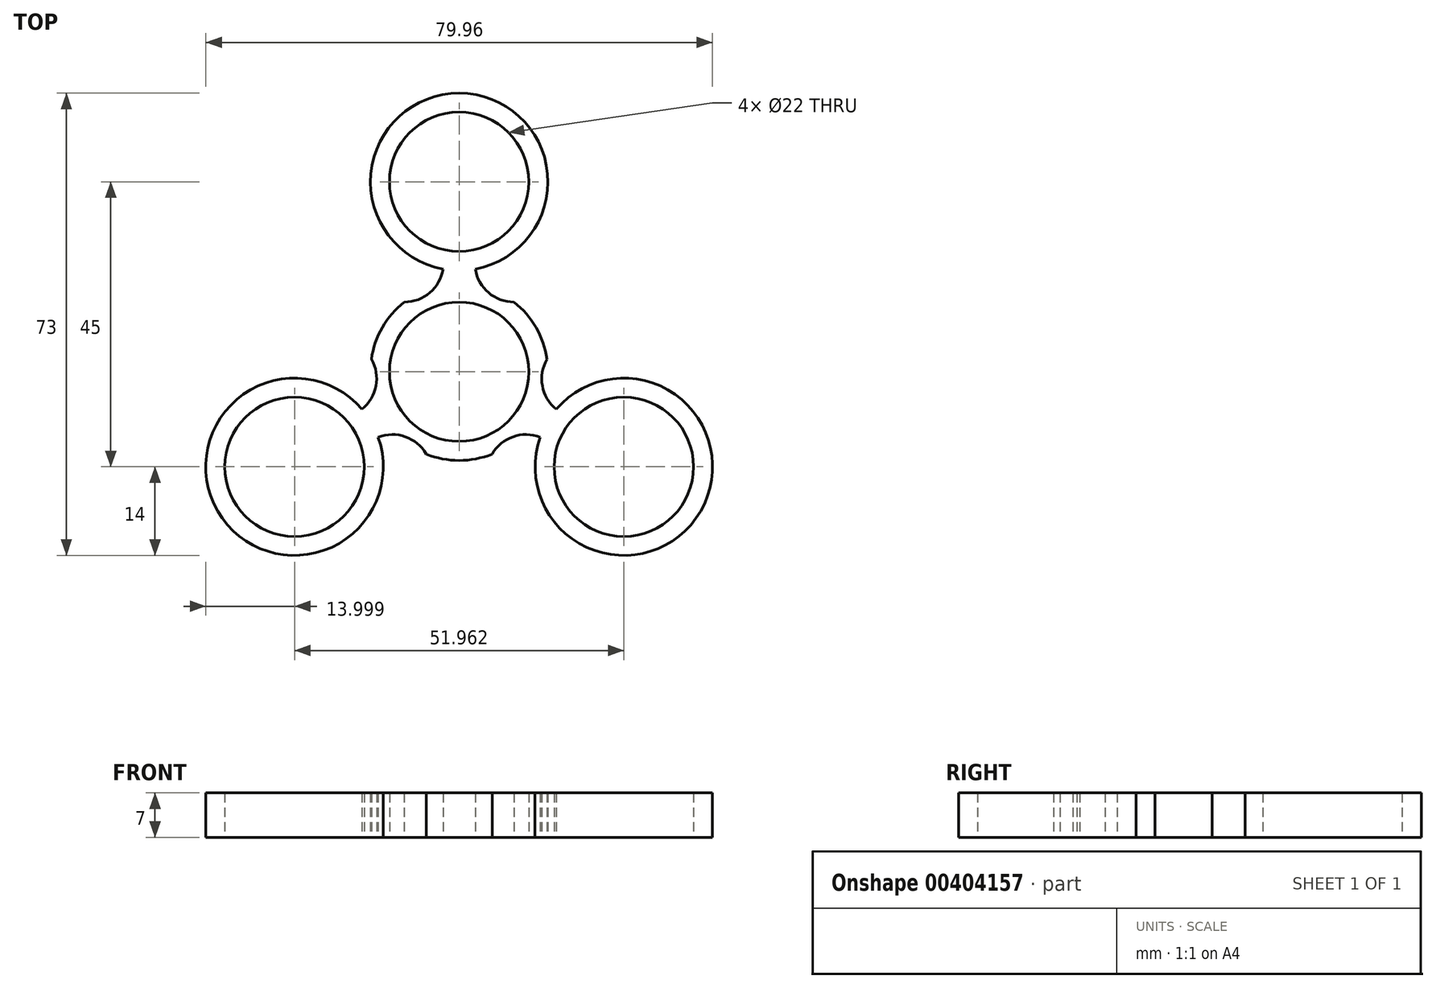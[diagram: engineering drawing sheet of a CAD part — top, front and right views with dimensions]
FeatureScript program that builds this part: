
annotation { "Feature Type Name" : "Feature", "Feature Type Description" : "" }
export const myFeature = defineFeature(function(context is Context, id is Id, definition is map)
    precondition{}
    {
        {
            var Q0;
            Q0=qCreatedBy(makeId("Top.planeOp"),FACE);
            var sketch = newSketch(context, id + "F0", { "sketchPlane" : qUnion([Q0])});
            skCircle(sketch, "E0", {"center": v(0, 0) * mm, "radius": 11 * mm});
            skCircle(sketch, "E1", {"center": v(0, 30) * mm, "radius": 11 * mm});
            skCircle(sketch, "E2.0", {"center": v(0, 30) * mm, "radius": 14 * mm});
            skLineSegment(sketch, "E3", {"start": v(0, 16.23) * mm, "end": v(-2.54, 16.23) * mm});
            skLineSegment(sketch, "E4.MirrorCS", {"start": v(0, 16.23) * mm, "end": v(2.54, 16.23) * mm});
            skArc(sketch, "E5", {"start": v(-8.66, 11) * mm, "mid": v(-5.87, 11.66) * mm, "end": v(-3.68, 13.5) * mm});
            skArc(sketch, "E6.MirrorCS", {"start": v(8.66, 11) * mm, "mid": v(4.63, 12.49) * mm, "end": v(2.54, 16.23) * mm});
            skArc(sketch, "E7", {"start": v(-3.68, 13.5) * mm, "mid": v(-2.95, 14.8) * mm, "end": v(-2.54, 16.23) * mm});
            skArc(sketch, "E8", {"start": v(-8.66, 11) * mm, "mid": v(-12.12, 7) * mm, "end": v(-13.86, 2) * mm});
            skCircle(sketch, "E9.1.0", {"center": v(-25.98, -15) * mm, "radius": 11 * mm});
            skArc(sketch, "E9.1.2", {"start": v(-5.2, -13) * mm, "mid": v(-7.16, -10.92) * mm, "end": v(-9.86, -9.94) * mm});
            skArc(sketch, "E9.1.3", {"start": v(-13.86, 2) * mm, "mid": v(-13.13, -2.23) * mm, "end": v(-15.33, -5.91) * mm});
            skCircle(sketch, "E9.1.5", {"center": v(-25.98, -15) * mm, "radius": 14 * mm});
            skLineSegment(sketch, "E9.1.6", {"start": v(-14.06, -8.12) * mm, "end": v(-12.79, -10.32) * mm});
            skLineSegment(sketch, "E9.1.7", {"start": v(-14.06, -8.12) * mm, "end": v(-15.33, -5.91) * mm});
            skArc(sketch, "E9.1.8", {"start": v(-9.86, -9.94) * mm, "mid": v(-11.34, -9.95) * mm, "end": v(-12.79, -10.32) * mm});
            skCircle(sketch, "E9.2.0", {"center": v(25.98, -15) * mm, "radius": 11 * mm});
            skArc(sketch, "E9.2.2", {"start": v(13.86, 2) * mm, "mid": v(13.04, -0.74) * mm, "end": v(13.54, -3.56) * mm});
            skArc(sketch, "E9.2.3", {"start": v(5.2, -13) * mm, "mid": v(8.5, -10.26) * mm, "end": v(12.79, -10.32) * mm});
            skCircle(sketch, "E9.2.5", {"center": v(25.98, -15) * mm, "radius": 14 * mm});
            skLineSegment(sketch, "E9.2.6", {"start": v(14.06, -8.12) * mm, "end": v(15.33, -5.91) * mm});
            skLineSegment(sketch, "E9.2.7", {"start": v(14.06, -8.12) * mm, "end": v(12.79, -10.32) * mm});
            skLineSegment(sketch, "E9.2.8", {"start": v(13.54, -3.56) * mm, "end": v(13.54, -3.56) * mm});
            skArc(sketch, "E10", {"start": v(13.86, 2) * mm, "mid": v(12.12, 7) * mm, "end": v(8.66, 11) * mm});
            skArc(sketch, "E11", {"start": v(13.54, -3.56) * mm, "mid": v(14.3, -4.85) * mm, "end": v(15.33, -5.91) * mm});
            skArc(sketch, "E12", {"start": v(-5.2, -13) * mm, "mid": v(0, -14) * mm, "end": v(5.2, -13) * mm});
            skSolve(sketch);
        }
        {
            var Q0;
            {var subQ2=sQuery(id+"F0.wireOp",EDGE,"E9.2.6");Q0=makeQuery(id+"F0.imprint","IMPRINT",FACE,{"disambiguationData":[TD([[makeQuery(id+"F0.imprint","IMPRINT",EDGE,{"derivedFrom":subQ2}),1.0]])]});}
            var Q1;
            Q1=makeQuery(id+"F0.imprint","IMPRINT",FACE,{"disambiguationData":[TD([[makeQuery(id+"F0.imprint","IMPRINT",EDGE,{"derivedFrom":sQuery(id+"F0.wireOp",EDGE,"E9.2.0")}),-1.0]])]});
            var Q2;
            Q2=makeQuery(id+"F0.imprint","IMPRINT",FACE,{"disambiguationData":[TD([[makeQuery(id+"F0.imprint","IMPRINT",EDGE,{"derivedFrom":sQuery(id+"F0.wireOp",EDGE,"E0")}),-1.0]])]});
            var Q3;
            {var subQ2=sQuery(id+"F0.wireOp",EDGE,"E9.1.6");Q3=makeQuery(id+"F0.imprint","IMPRINT",FACE,{"disambiguationData":[TD([[makeQuery(id+"F0.imprint","IMPRINT",EDGE,{"derivedFrom":subQ2}),1.0]])]});}
            var Q4;
            Q4=makeQuery(id+"F0.imprint","IMPRINT",FACE,{"disambiguationData":[TD([[makeQuery(id+"F0.imprint","IMPRINT",EDGE,{"derivedFrom":sQuery(id+"F0.wireOp",EDGE,"E9.1.0")}),-1.0]])]});
            var Q5;
            Q5=makeQuery(id+"F0.imprint","IMPRINT",FACE,{"disambiguationData":[TD([[makeQuery(id+"F0.imprint","IMPRINT",EDGE,{"derivedFrom":sQuery(id+"F0.wireOp",EDGE,"E1")}),-1.0]])]});
            var Q6;
            {var subQ0=sQuery(id+"F0.wireOp",EDGE,"E3");Q6=makeQuery(id+"F0.imprint","IMPRINT",FACE,{"disambiguationData":[TD([[makeQuery(id+"F0.imprint","IMPRINT",EDGE,{"derivedFrom":subQ0}),1.0]])]});}
            extrude(context, id + "F1", {"entities" : qUnion([Q0, Q1, Q2, Q3, Q4, Q5, Q6]), "depth" : 7 * mm});
        }
    });
